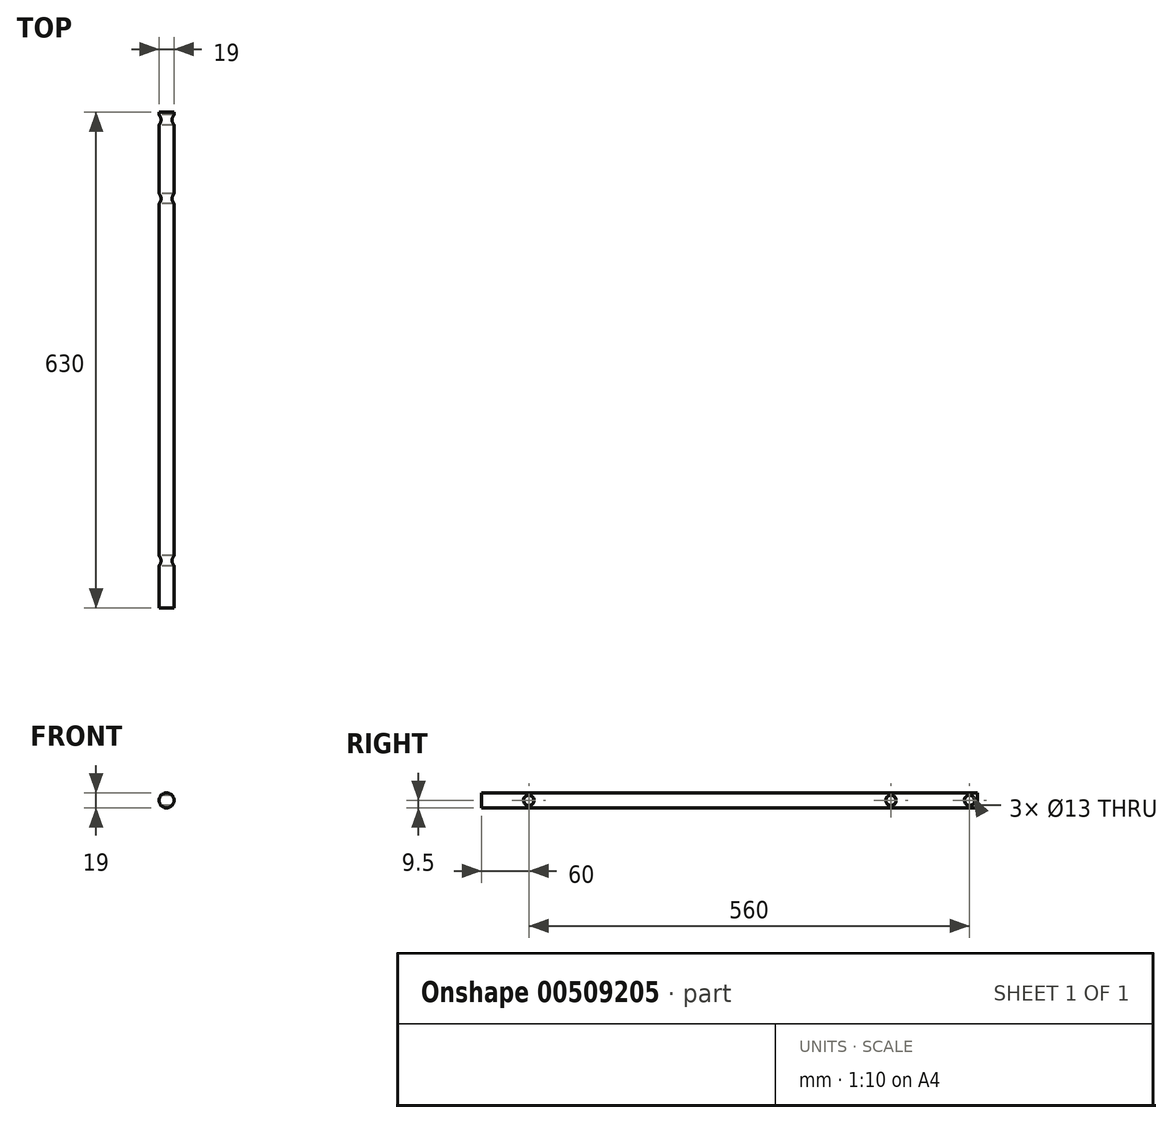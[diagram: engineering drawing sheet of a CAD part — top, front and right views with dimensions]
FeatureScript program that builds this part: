
annotation { "Feature Type Name" : "Feature", "Feature Type Description" : "" }
export const myFeature = defineFeature(function(context is Context, id is Id, definition is map)
    precondition{}
    {
        {
            var Q0;
            Q0=qCreatedBy(makeId("Front.planeOp"),FACE);
            var sketch = newSketch(context, id + "F0", { "sketchPlane" : qUnion([Q0])});
            skCircle(sketch, "E0", {"center": v(0, 0) * mm, "radius": 9.5 * mm});
            skSolve(sketch);
        }
        {
            var Q0;
            Q0=qSketchRegion(id+"F0",true);
            extrude(context, id + "F1", {"entities" : qUnion([Q0]), "depth" : 630 * mm});
        }
        {
            var Q0;
            Q0=qCreatedBy(makeId("Right.planeOp"),FACE);
            var sketch = newSketch(context, id + "F2", { "sketchPlane" : qUnion([Q0])});
            skCircle(sketch, "E1", {"center": v(-10, 0) * mm, "radius": 6.5 * mm});
            skCircle(sketch, "E2", {"center": v(-110, 0) * mm, "radius": 6.5 * mm});
            skCircle(sketch, "E3", {"center": v(-570, 0) * mm, "radius": 6.5 * mm});
            skSolve(sketch);
        }
        {
            var Q0;
            Q0=qSketchRegion(id+"F2",true);
            extrude(context, id + "F3", {"entities" : qUnion([Q0]), "operationType" : NewBodyOperationType.REMOVE, "depth" : 25 * mm, "hasSecondDirection" : true, "secondDirectionOppositeDirection" : true, "secondDirectionDepth" : 25 * mm});
        }
    });
